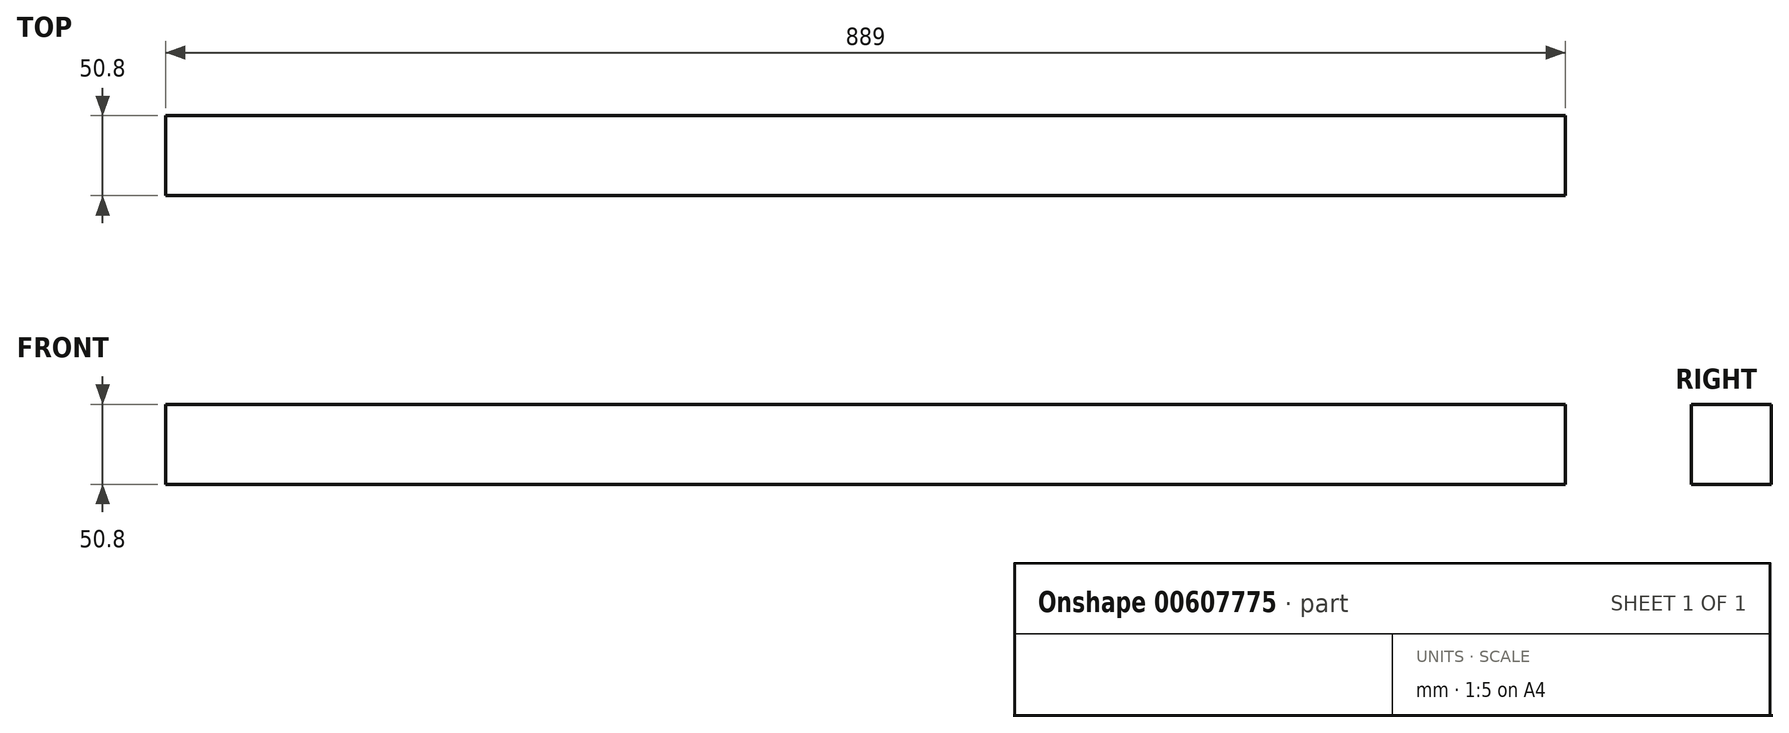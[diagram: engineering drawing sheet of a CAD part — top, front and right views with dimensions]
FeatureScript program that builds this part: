
annotation { "Feature Type Name" : "Feature", "Feature Type Description" : "" }
export const myFeature = defineFeature(function(context is Context, id is Id, definition is map)
    precondition{}
    {
        {
            var Q0;
            Q0=qCreatedBy(makeId("Front.planeOp"),FACE);
            var sketch = newSketch(context, id + "F0", { "sketchPlane" : qUnion([Q0])});
            skLineSegment(sketch, "E0.bottom", {"start": v(0, 0) * mm, "end": v(-889, 0) * mm});
            skLineSegment(sketch, "E0.top", {"start": v(0, 50.8) * mm, "end": v(-889, 50.8) * mm});
            skLineSegment(sketch, "E0.left", {"start": v(0, 0) * mm, "end": v(0, 50.8) * mm});
            skLineSegment(sketch, "E0.right", {"start": v(-889, 0) * mm, "end": v(-889, 50.8) * mm});
            skSolve(sketch);
        }
        {
            var Q0;
            Q0 = qSketchRegion(id + "F0", true);
            extrude(context, id + "F1", {"entities" : qUnion([Q0]), "depth" : 50.8 * mm, "offsetDistance" : 25.4 * mm});
        }
    });
